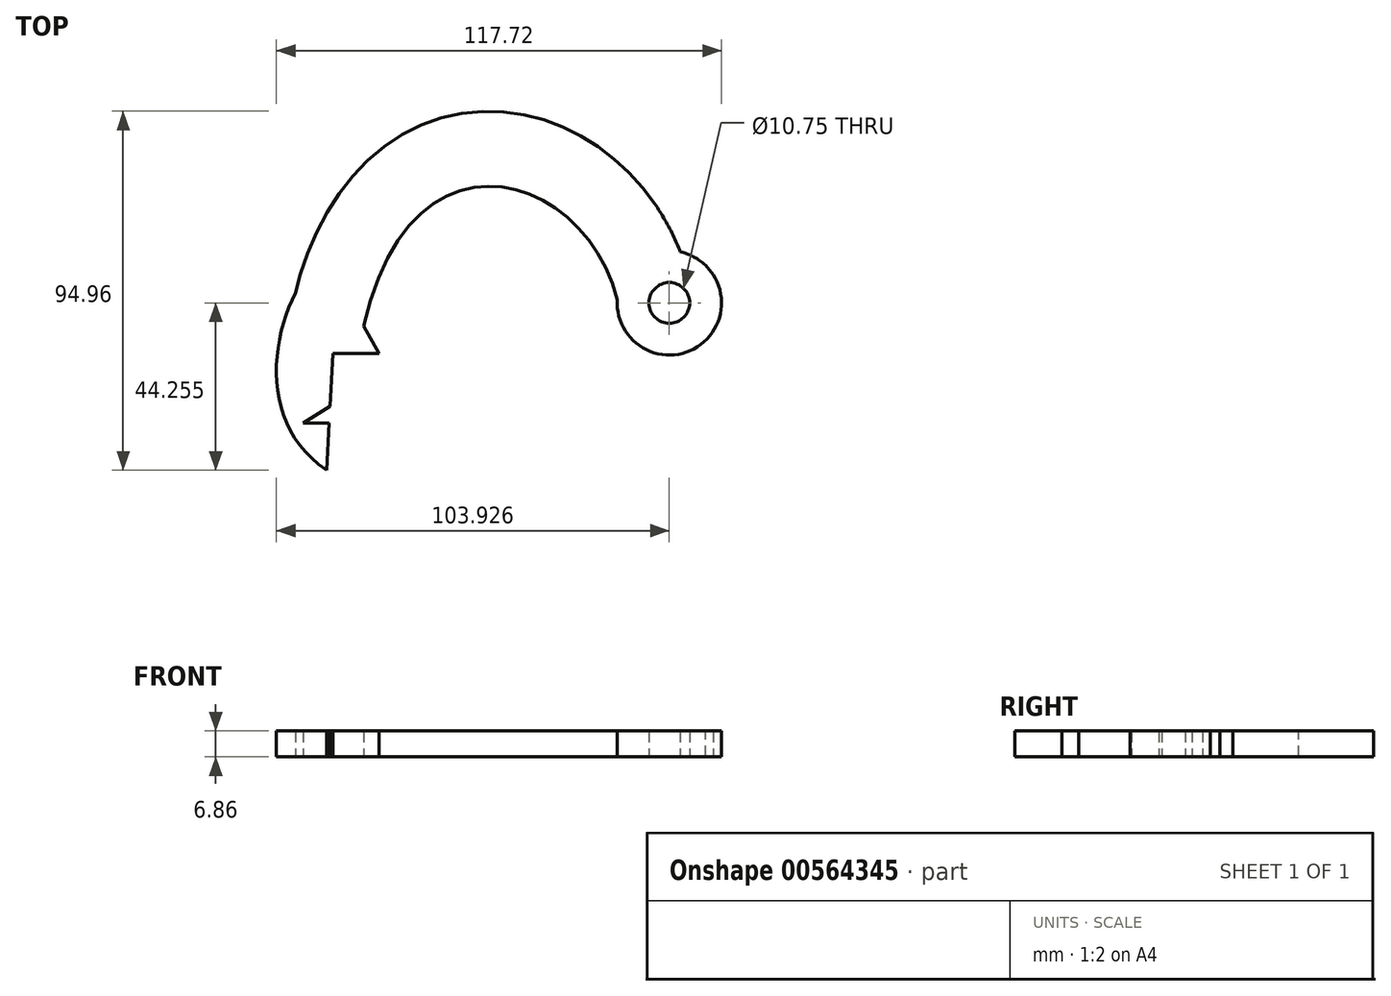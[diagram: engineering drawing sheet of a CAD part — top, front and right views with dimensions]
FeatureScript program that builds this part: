
annotation { "Feature Type Name" : "Feature", "Feature Type Description" : "" }
export const myFeature = defineFeature(function(context is Context, id is Id, definition is map)
    precondition{}
    {
        {
            var Q0;
            Q0=qCreatedBy(makeId("Top.planeOp"),FACE);
            var sketch = newSketch(context, id + "F0", { "sketchPlane" : qUnion([Q0])});
            skCircle(sketch, "E0", {"center": v(46.2, 56.85) * mm, "radius": 5.38 * mm});
            skCircle(sketch, "E1", {"center": v(46.2, 56.85) * mm, "radius": 13.8 * mm});
            skFitSpline(sketch, "E2", {"points": [v(32.44, 57.71) * mm, v(-34.57, 50.66) * mm], "startDerivative": vector(-25.96, 103.12) * mm, "endDerivative": vector(-35.59, -164.59) * mm});
            skFitSpline(sketch, "E3", {"points": [v(38.63, 87.6) * mm, v(57.8, 64.33) * mm], "startDerivative": vector(19.17, -23.29) * mm, "endDerivative": vector(19.17, -23.29) * mm});
            skFitSpline(sketch, "E4", {"points": [v(-52.46, 59.92) * mm, v(-44.46, 12.6) * mm], "startDerivative": vector(-22.6, -43.5) * mm, "endDerivative": vector(50.03, -33.75) * mm});
            skLineSegment(sketch, "E5", {"start": v(-44.46, 12.6) * mm, "end": v(-43.79, 25.11) * mm});
            skLineSegment(sketch, "E6", {"start": v(-42.8, 43.5) * mm, "end": v(-30.62, 43.5) * mm});
            skLineSegment(sketch, "E7", {"start": v(-30.62, 43.5) * mm, "end": v(-34.57, 50.66) * mm});
            skPoint(sketch, "E8.start.orphan", {"position": v(0, 79.19) * mm});
            skFitSpline(sketch, "E9.trimOffspring", {"points": [v(51.4, 62.48) * mm, v(50.63, 65.56) * mm, v(48.65, 71.52) * mm, v(44.52, 79.7) * mm, v(39.36, 87.05) * mm, v(33.28, 93.47) * mm, v(26.36, 98.87) * mm, v(18.67, 103.12) * mm, v(10.27, 106.07) * mm, v(1.3, 107.47) * mm, v(-8.04, 107.1) * mm, v(-17.35, 104.73) * mm, v(-26.16, 100.35) * mm, v(-34.06, 94.11) * mm, v(-40.8, 86.3) * mm, v(-46.31, 77.13) * mm, v(-50.66, 66.7) * mm, v(-52.8, 58.91) * mm, v(-53.7, 54.8) * mm]});
            skLineSegment(sketch, "E10", {"start": v(-43.55, 29.5) * mm, "end": v(-50.57, 25.11) * mm});
            skLineSegment(sketch, "E11", {"start": v(-50.57, 25.11) * mm, "end": v(-43.79, 25.11) * mm});
            skLineSegment(sketch, "E12.trimOffspring", {"start": v(-43.55, 29.5) * mm, "end": v(-42.8, 43.5) * mm});
            skSolve(sketch);
        }
        {
            var Q0;
            {var subQ4=sQuery(id+"F0.wireOp",EDGE,"E2");Q0=makeQuery(id+"F0.imprint","IMPRINT",FACE,{"disambiguationData":[TD([[makeQuery(id+"F0.imprint","IMPRINT",EDGE,{"derivedFrom":subQ4}),-1.0]])]});}
            var Q1;
            Q1=makeQuery(id+"F0.imprint","IMPRINT",FACE,{"disambiguationData":[TD([[makeQuery(id+"F0.imprint","IMPRINT",EDGE,{"derivedFrom":sQuery(id+"F0.wireOp",EDGE,"E0")}),-1.0]])]});
            extrude(context, id + "F1", {"entities" : qUnion([Q0, Q1]), "depth" : 6.86 * mm, "offsetDistance" : 25.4 * mm});
        }
    });
